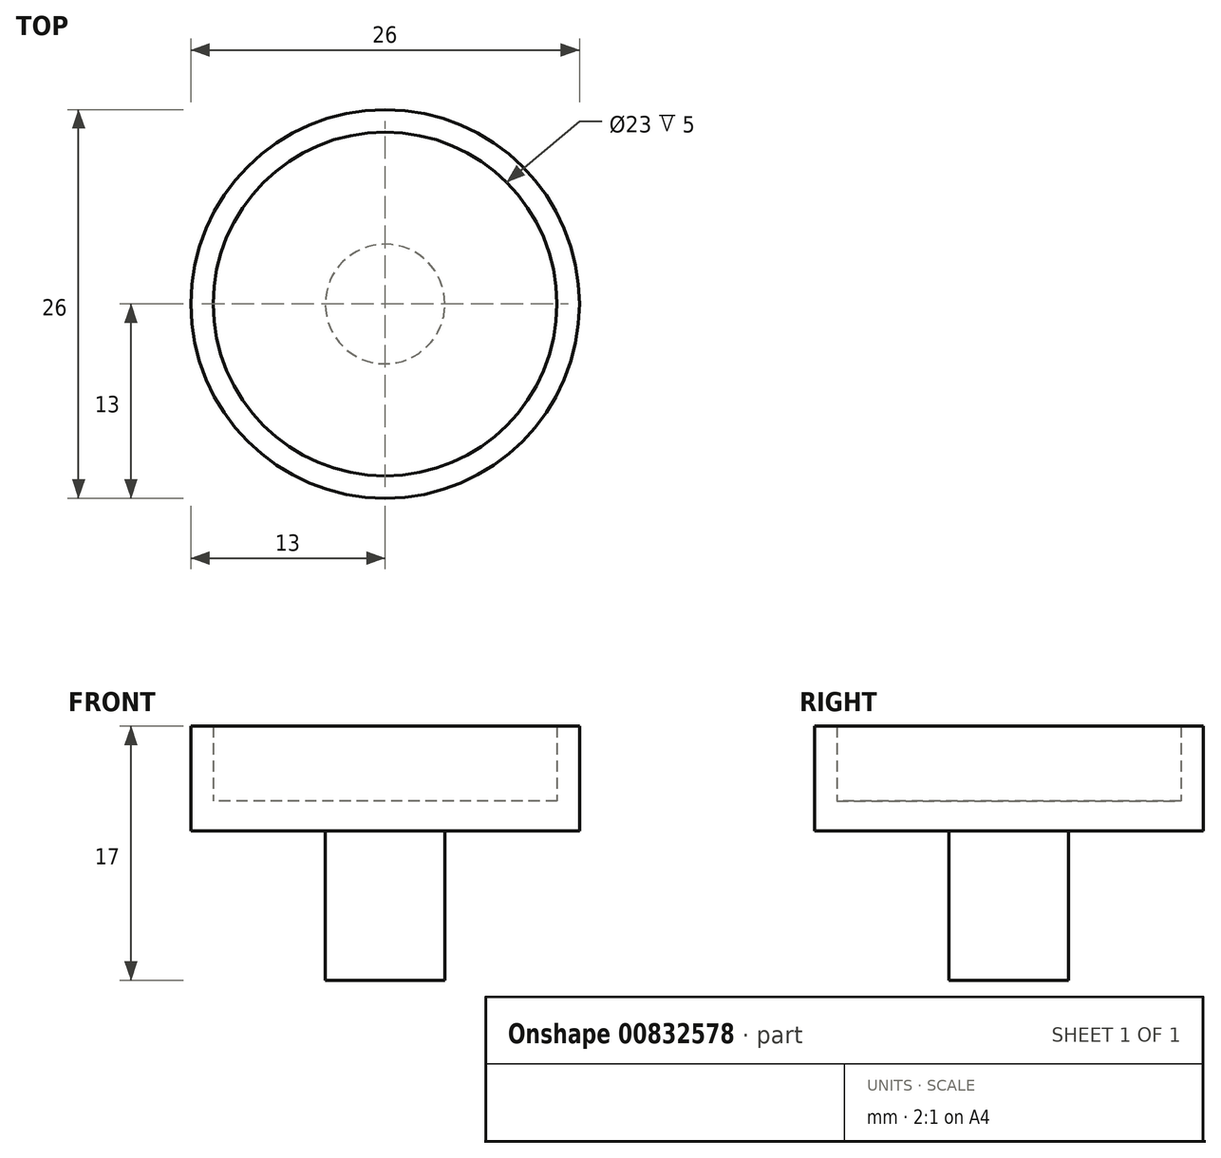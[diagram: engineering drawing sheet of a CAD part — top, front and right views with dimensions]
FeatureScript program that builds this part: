
annotation { "Feature Type Name" : "Feature", "Feature Type Description" : "" }
export const myFeature = defineFeature(function(context is Context, id is Id, definition is map)
    precondition{}
    {
        {
            var Q0;
            Q0=qCreatedBy(makeId("Top.planeOp"),FACE);
            var sketch = newSketch(context, id + "F0", { "sketchPlane" : qUnion([Q0])});
            skCircle(sketch, "E0", {"center": v(0, 0) * mm, "radius": 4 * mm});
            skSolve(sketch);
        }
        {
            var Q0;
            Q0=makeQuery(id+"F0.imprint","IMPRINT",FACE,{"disambiguationData":[TD([[makeQuery(id+"F0.imprint","IMPRINT",EDGE,{"derivedFrom":sQuery(id+"F0.wireOp",EDGE,"E0")}),1.0]])]});
            extrude(context, id + "F1", {"entities" : qUnion([Q0]), "oppositeDirection" : true, "depth" : 10 * mm, "offsetDistance" : 25 * mm});
        }
        {
            var Q0;
            Q0=makeQuery(id+"F1.opExtrude","CAP_FACE",FACE,{"disambiguationData":[OSD([sQuery(id+"F0.wireOp",EDGE,"E0")])],"isStart":true});
            var sketch = newSketch(context, id + "F2", { "sketchPlane" : qUnion([Q0])});
            skCircle(sketch, "E1", {"center": v(0, 0) * mm, "radius": 11.5 * mm});
            skCircle(sketch, "E2", {"center": v(0, 0) * mm, "radius": 13 * mm});
            skSolve(sketch);
        }
        {
            var Q0;
            Q0=makeQuery(id+"F2.imprint","IMPRINT",FACE,{"disambiguationData":[TD([[makeQuery(id+"F2.imprint","IMPRINT",EDGE,{"derivedFrom":sQuery(id+"F2.wireOp",EDGE,"E1")}),1.0]])]});
            var Q1;
            Q1=makeQuery(id+"F2.imprint","IMPRINT",FACE,{"disambiguationData":[TD([[makeQuery(id+"F2.imprint","IMPRINT",EDGE,{"derivedFrom":makeQuery(id+"F1.opExtrude","CAP_EDGE",EDGE,{"disambiguationData":[OSD([sQuery(id+"F0.wireOp",EDGE,"E0")])],"isStart":true})}),1.0]])]});
            extrude(context, id + "F3", {"entities" : qUnion([Q0, Q1]), "depth" : 2 * mm, "offsetDistance" : 25 * mm});
        }
        {
            var Q0;
            Q0=makeQuery(id+"F2.imprint","IMPRINT",FACE,{"disambiguationData":[TD([[makeQuery(id+"F2.imprint","IMPRINT",EDGE,{"derivedFrom":sQuery(id+"F2.wireOp",EDGE,"E1")}),-1.0]])]});
            extrude(context, id + "F4", {"entities" : qUnion([Q0]), "operationType" : NewBodyOperationType.ADD, "depth" : 7 * mm, "offsetDistance" : 25 * mm});
        }
    });
